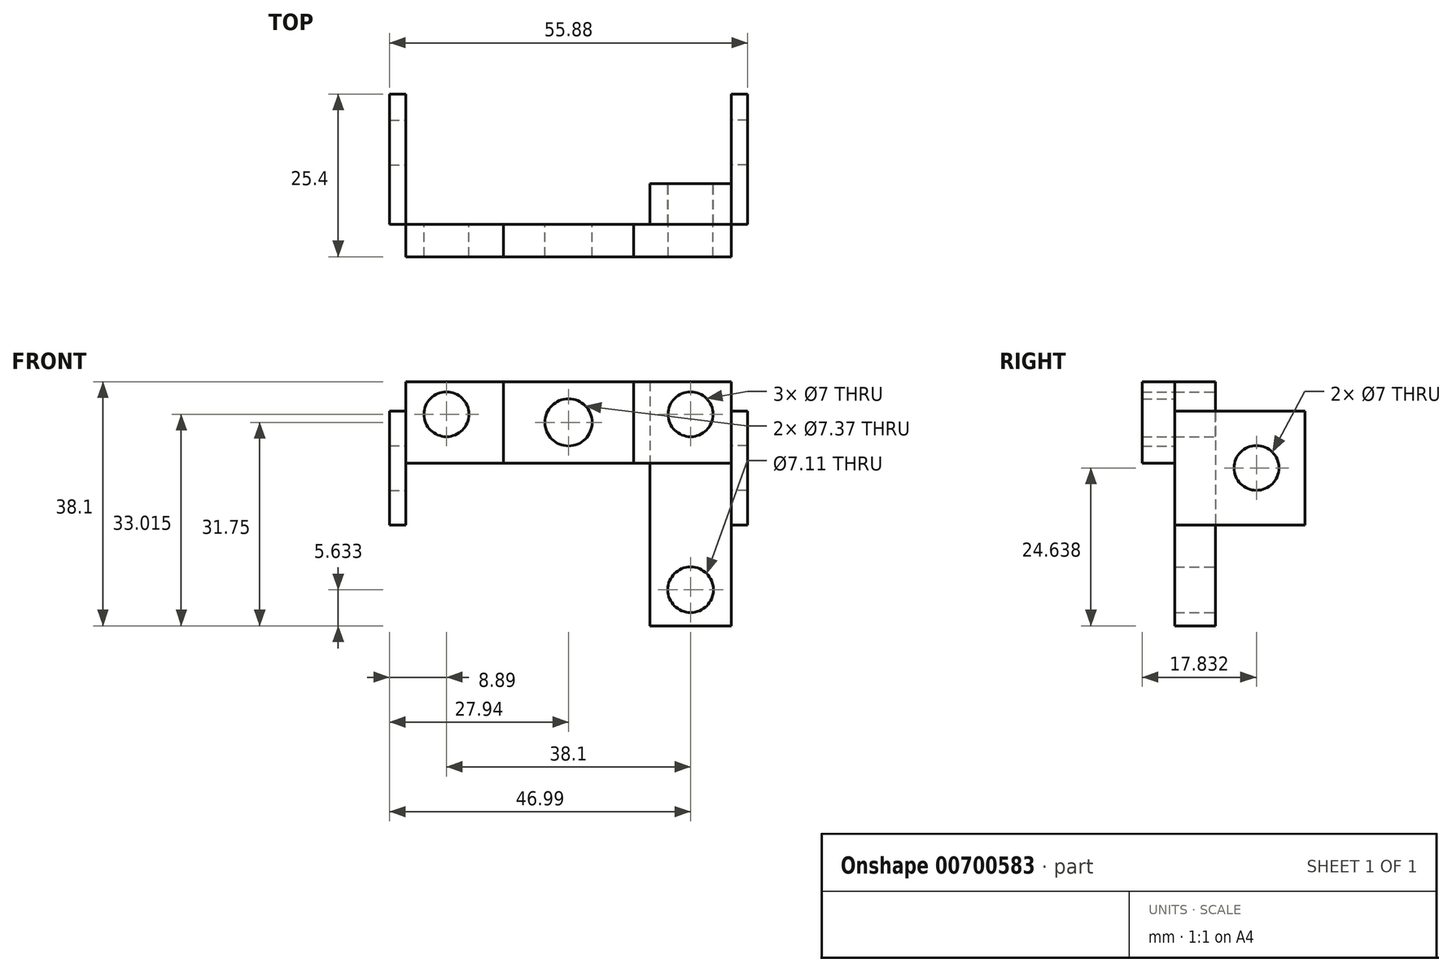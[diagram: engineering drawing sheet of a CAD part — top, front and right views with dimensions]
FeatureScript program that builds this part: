
annotation { "Feature Type Name" : "Feature", "Feature Type Description" : "" }
export const myFeature = defineFeature(function(context is Context, id is Id, definition is map)
    precondition{}
    {
        {
            var Q0;
            Q0=qCreatedBy(makeId("Front.planeOp"),FACE);
            var sketch = newSketch(context, id + "F0", { "sketchPlane" : qUnion([Q0])});
            skLineSegment(sketch, "E0.bottom", {"start": v(12.7, 38.1) * mm, "end": v(25.4, 38.1) * mm});
            skLineSegment(sketch, "E0.top", {"start": v(12.7, 0) * mm, "end": v(25.4, 0) * mm});
            skLineSegment(sketch, "E0.left", {"start": v(12.7, 38.1) * mm, "end": v(12.7, 0) * mm});
            skLineSegment(sketch, "E0.right", {"start": v(25.4, 38.1) * mm, "end": v(25.4, 0) * mm});
            skCircle(sketch, "E1", {"center": v(19.05, 33.01) * mm, "radius": 3.5 * mm});
            skPoint(sketch, "E1.centerSnap0", {"position": v(19.05, 38.1) * mm});
            skLineSegment(sketch, "E2", {"start": v(19.05, 0) * mm, "end": v(19.05, 38.1) * mm, "construction": true});
            skCircle(sketch, "E3", {"center": v(19.05, 5.63) * mm, "radius": 3.56 * mm});
            skSolve(sketch);
        }
        {
            var Q0;
            Q0 = qSketchRegion(id + "F0", true);
            extrude(context, id + "F1", {"entities" : qUnion([Q0]), "depth" : 6.35 * mm, "offsetDistance" : 25.4 * mm});
        }
        {
            var Q0;
            Q0=makeQuery(id+"F1.opExtrude","CAP_FACE",FACE,{"disambiguationData":[OSD([sQuery(id+"F0.wireOp",EDGE,"E0.bottom"),sQuery(id+"F0.wireOp",EDGE,"E0.top"),sQuery(id+"F0.wireOp",EDGE,"E0.left"),sQuery(id+"F0.wireOp",EDGE,"E0.right"),sQuery(id+"F0.wireOp",EDGE,"E1")])],"isStart":false});
            var sketch = newSketch(context, id + "F2", { "sketchPlane" : qUnion([Q0])});
            skCircle(sketch, "E4", {"center": v(19.05, 33.01) * mm, "radius": 3.5 * mm});
            skLineSegment(sketch, "E5", {"start": v(25.4, 19.05) * mm, "end": v(25.4, -4.34) * mm, "construction": true});
            skLineSegment(sketch, "E6", {"start": v(25.4, -4.34) * mm, "end": v(-9.24, -4.34) * mm, "construction": true});
            skLineSegment(sketch, "E7", {"start": v(-10.16, 25.4) * mm, "end": v(25.4, 25.4) * mm, "construction": true});
            skLineSegment(sketch, "E8.bottom", {"start": v(25.4, 25.4) * mm, "end": v(-10.16, 25.4) * mm});
            skLineSegment(sketch, "E8.top", {"start": v(25.4, 38.1) * mm, "end": v(-10.16, 38.1) * mm});
            skLineSegment(sketch, "E8.left", {"start": v(25.4, 25.4) * mm, "end": v(25.4, 38.1) * mm});
            skLineSegment(sketch, "E8.right", {"start": v(-10.16, 25.4) * mm, "end": v(-10.16, 38.1) * mm});
            skCircle(sketch, "E9", {"center": v(0, 31.75) * mm, "radius": 3.68 * mm});
            skPoint(sketch, "E9.centerSnap0", {"position": v(-10.16, 31.75) * mm});
            skSolve(sketch);
        }
        {
            var Q0;
            Q0 = qSketchRegion(id + "F2", true);
            extrude(context, id + "F3", {"entities" : qUnion([Q0]), "depth" : 5.08 * mm, "offsetDistance" : 25.4 * mm});
        }
        {
            var Q0;
            Q0=makeQuery(id+"F3.opExtrude","SWEPT_BODY",BODY,{"disambiguationData":[OSD([sQuery(id+"F2.wireOp",EDGE,"FvGwd2aR-DdLF-ptD5-V0zB-aNURW71SK1EE.bottom"),sQuery(id+"F2.wireOp",EDGE,"FvGwd2aR-DdLF-ptD5-V0zB-aNURW71SK1EE.top"),sQuery(id+"F2.wireOp",EDGE,"FvGwd2aR-DdLF-ptD5-V0zB-aNURW71SK1EE.left"),sQuery(id+"F2.wireOp",EDGE,"FvGwd2aR-DdLF-ptD5-V0zB-aNURW71SK1EE.right"),sQuery(id+"F2.wireOp",EDGE,"E4")])]});
            var Q1;
            Q1=qCreatedBy(makeId("Right.planeOp"),FACE);
            mirror(context, id + "F4", {"entities" : qUnion([Q0]), "mirrorPlane" : qUnion([Q1])});
        }
        {
            var Q0;
            Q0=makeQuery(id+"F1.opExtrude","SWEPT_BODY",BODY,{"disambiguationData":[OSD([sQuery(id+"F0.wireOp",EDGE,"E0.bottom"),sQuery(id+"F0.wireOp",EDGE,"E0.top"),sQuery(id+"F0.wireOp",EDGE,"E0.left"),sQuery(id+"F0.wireOp",EDGE,"E0.right"),sQuery(id+"F0.wireOp",EDGE,"E1")])]});
            var Q1;
            Q1=qCreatedBy(makeId("Right.planeOp"),FACE);
            mirror(context, id + "F5", {"entities" : qUnion([Q0]), "mirrorPlane" : qUnion([Q1])});
        }
        {
            var Q0;
            Q0=makeQuery(id+"F1.opExtrude","SWEPT_FACE",FACE,{"disambiguationData":[OSD([sQuery(id+"F0.wireOp",EDGE,"E0.right")])]});
            var sketch = newSketch(context, id + "F6", { "sketchPlane" : qUnion([Q0])});
            skLineSegment(sketch, "E10", {"start": v(-3.3, 24.64) * mm, "end": v(3.05, 24.64) * mm, "construction": true});
            skLineSegment(sketch, "E11.bottom", {"start": v(-6.35, 15.75) * mm, "end": v(13.97, 15.75) * mm});
            skLineSegment(sketch, "E11.top", {"start": v(-6.35, 33.53) * mm, "end": v(13.97, 33.53) * mm});
            skLineSegment(sketch, "E11.left", {"start": v(-6.35, 15.75) * mm, "end": v(-6.35, 33.53) * mm});
            skLineSegment(sketch, "E11.right", {"start": v(13.97, 15.75) * mm, "end": v(13.97, 33.53) * mm});
            skCircle(sketch, "E12", {"center": v(6.4, 24.64) * mm, "radius": 3.5 * mm});
            skSolve(sketch);
        }
        {
            var Q0;
            Q0 = qSketchRegion(id + "F6", true);
            extrude(context, id + "F7", {"entities" : qUnion([Q0]), "depth" : 2.54 * mm, "offsetDistance" : 25.4 * mm});
        }
        {
            var Q0;
            Q0=makeQuery(id+"F7.opExtrude","SWEPT_BODY",BODY,{"disambiguationData":[OSD([sQuery(id+"F6.wireOp",EDGE,"E11.bottom"),sQuery(id+"F6.wireOp",EDGE,"E11.top"),sQuery(id+"F6.wireOp",EDGE,"E11.left"),sQuery(id+"F6.wireOp",EDGE,"E11.right")])]});
            var Q1;
            Q1=qCreatedBy(makeId("Right.planeOp"),FACE);
            mirror(context, id + "F8", {"entities" : qUnion([Q0]), "mirrorPlane" : qUnion([Q1])});
        }
        {
            var Q0;
            Q0=makeQuery(id+"F5.opPattern","COPY",BODY,{"derivedFrom":makeQuery(id+"F1.opExtrude","SWEPT_BODY",BODY,{"disambiguationData":[OSD([sQuery(id+"F0.wireOp",EDGE,"E0.bottom"),sQuery(id+"F0.wireOp",EDGE,"E0.top"),sQuery(id+"F0.wireOp",EDGE,"E0.left"),sQuery(id+"F0.wireOp",EDGE,"E0.right"),sQuery(id+"F0.wireOp",EDGE,"E1")])]}),"instanceName":"1"});
            deleteBodies(context, id + "F9", {"entities" : qUnion([Q0])});
        }
    });
